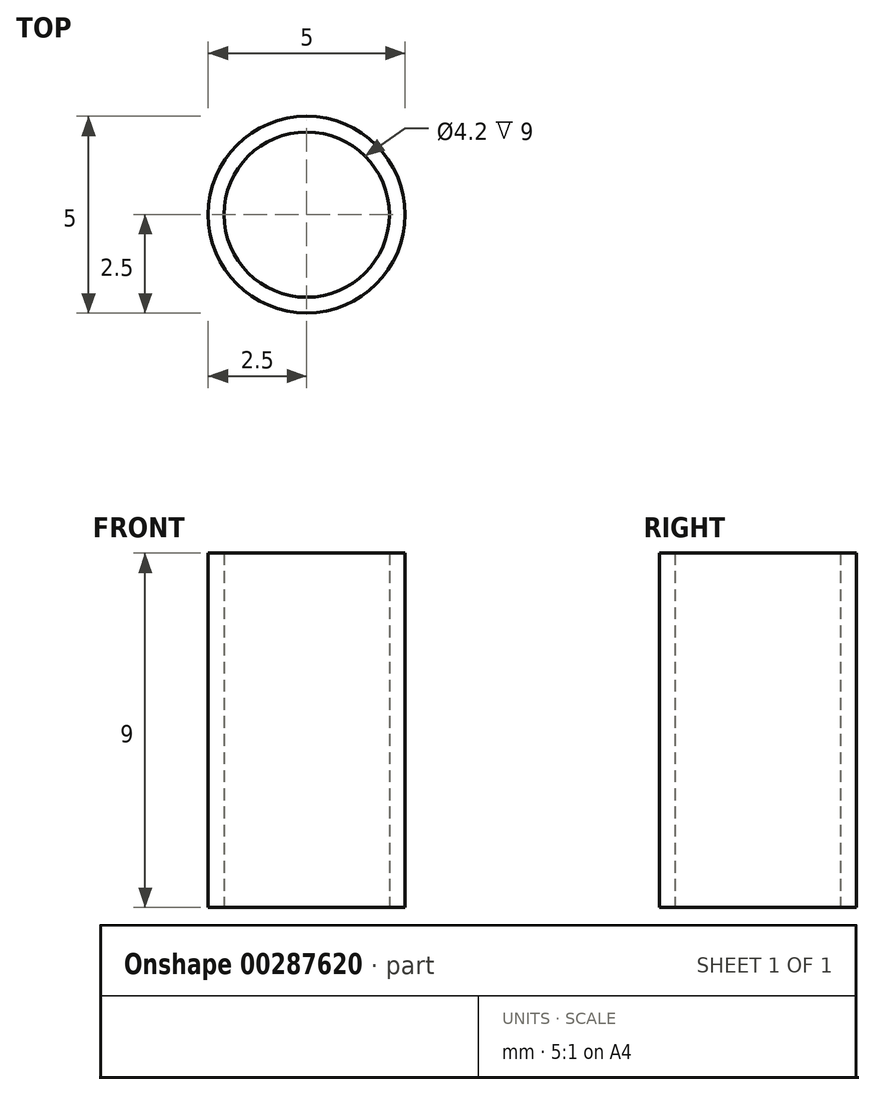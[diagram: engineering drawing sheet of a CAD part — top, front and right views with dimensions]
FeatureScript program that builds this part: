
annotation { "Feature Type Name" : "Feature", "Feature Type Description" : "" }
export const myFeature = defineFeature(function(context is Context, id is Id, definition is map)
    precondition{}
    {
        {
            var Q0;
            Q0=qCreatedBy(makeId("Top.planeOp"),FACE);
            var sketch = newSketch(context, id + "F0", { "sketchPlane" : qUnion([Q0])});
            skCircle(sketch, "E0", {"center": v(0, 0) * mm, "radius": 2.5 * mm});
            skCircle(sketch, "E1", {"center": v(0, 0) * mm, "radius": 2.1 * mm});
            skSolve(sketch);
        }
        {
            var Q0;
            Q0=makeQuery(id+"F0.imprint","IMPRINT",FACE,{"disambiguationData":[TD([[makeQuery(id+"F0.imprint","IMPRINT",EDGE,{"derivedFrom":sQuery(id+"F0.wireOp",EDGE,"E0")}),1.0]])]});
            extrude(context, id + "F1", {"entities" : qUnion([Q0]), "depth" : 9 * mm, "offsetDistance" : 25 * mm});
        }
    });
